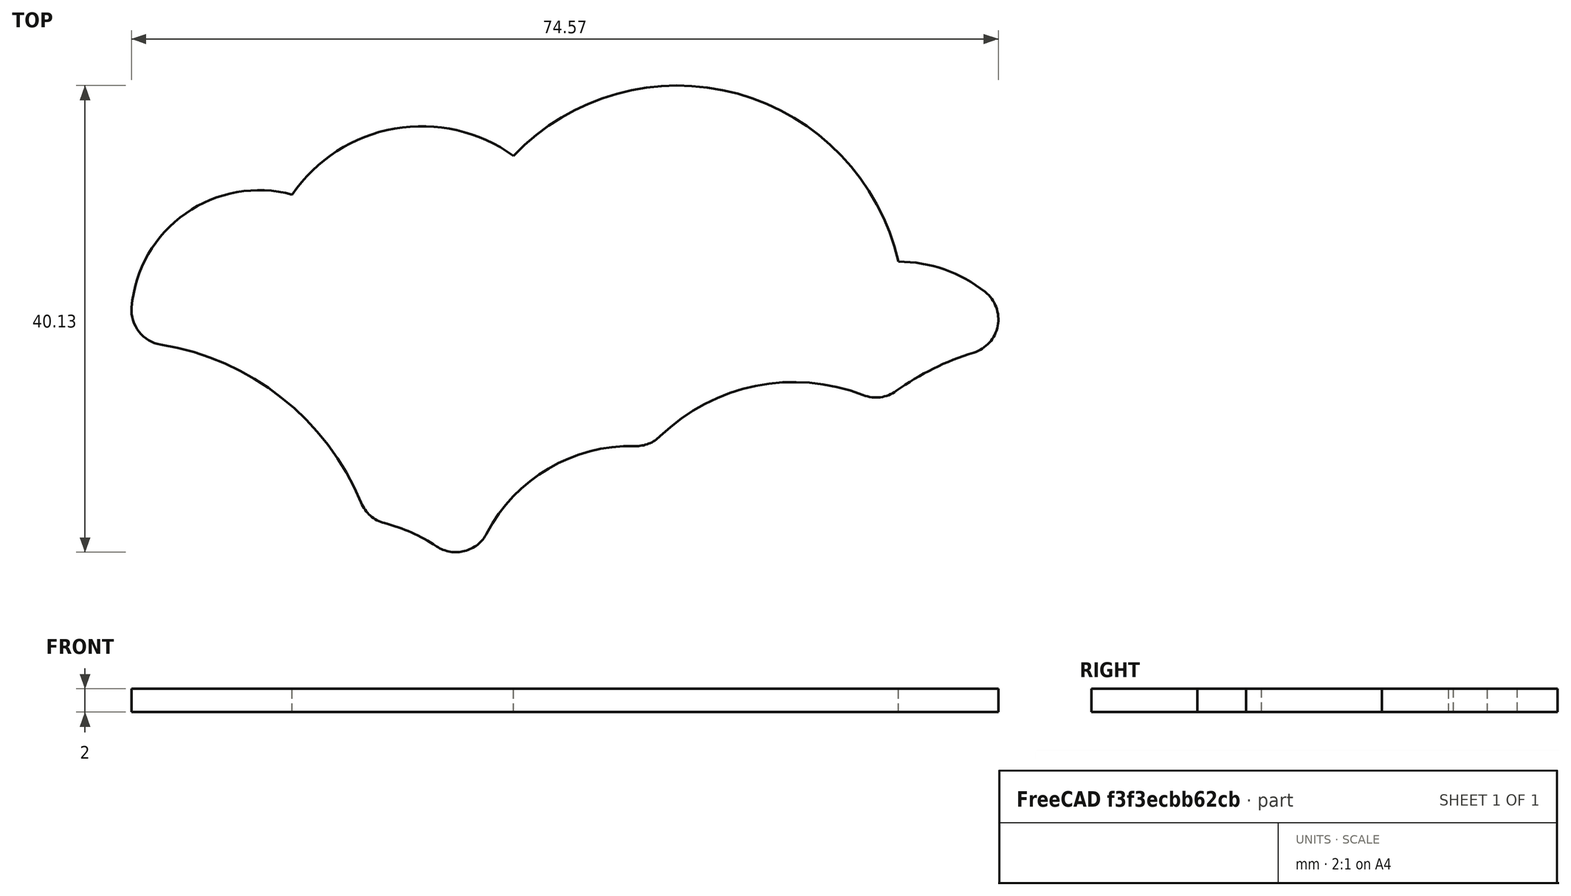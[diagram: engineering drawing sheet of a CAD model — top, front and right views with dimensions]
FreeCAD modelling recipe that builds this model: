
FCSTD DOCUMENT  (FreeCAD 0.16R6712 (Git))
Label: steam_badge2
License: All rights reserved
LicenseURL: http://en.wikipedia.org/wiki/All_rights_reserved
objects: Sketcher::SketchObject×1, Part::Feature×1, PartDesign::Pad×1
note: 4 computed .brp shape members not serialized (recipe doc carries the construction recipe); baked Part::Feature solids carry a one-line shape summary decoded from their .brp

FEATURE [Sketcher::SketchObject] Sketch
  sketch-geometry (15):
    g0: ArcOfCircle CenterX=-28 CenterY=3.5 CenterZ=0 NormalX=0 NormalY=0 NormalZ=1 Radius=11 StartAngle=1.30799 EndAngle=3.05653
    g1: ArcOfCircle CenterX=-14 CenterY=6.5 CenterZ=0 NormalX=0 NormalY=0 NormalZ=1 Radius=13.5 StartAngle=0.946866 EndAngle=2.54163
    g2: ArcOfCircle CenterX=8 CenterY=4 CenterZ=0 NormalX=0 NormalY=0 NormalZ=1 Radius=19.5 StartAngle=0.225496 EndAngle=2.38
    g3: ArcOfCircle CenterX=27 CenterY=-3.64 CenterZ=0 NormalX=0 NormalY=0 NormalZ=1 Radius=12 StartAngle=0.898843 EndAngle=1.57027
    g4: ArcOfCircle CenterX=-40 CenterY=-21 CenterZ=0 NormalX=0 NormalY=0 NormalZ=1 Radius=22.5 StartAngle=0.393398 EndAngle=1.41213
    g5: ArcOfCircle CenterX=-21 CenterY=-28.64 CenterZ=0 NormalX=0 NormalY=0 NormalZ=1 Radius=15 StartAngle=0.986285 EndAngle=1.31513
    g6: ArcOfCircle CenterX=4 CenterY=-21.5 CenterZ=0 NormalX=0 NormalY=0 NormalZ=1 Radius=14 StartAngle=1.54604 EndAngle=2.66017
    g7: ArcOfCircle CenterX=18 CenterY=-18.5 CenterZ=0 NormalX=0 NormalY=0 NormalZ=1 Radius=16.5 StartAngle=1.19974 EndAngle=2.34113
    g8: ArcOfCircle CenterX=40 CenterY=-21 CenterZ=0 NormalX=0 NormalY=0 NormalZ=1 Radius=22.5 StartAngle=1.86512 EndAngle=2.19624
    g9: ArcOfCircle CenterX=-35.9711 CenterY=4.17971 CenterZ=0 NormalX=0 NormalY=0 NormalZ=1 Radius=3 StartAngle=3.05653 EndAngle=4.55373
    g10: ArcOfCircle CenterX=-11.0677 CenterY=-13.6283 CenterZ=0 NormalX=0 NormalY=0 NormalZ=1 Radius=3 StartAngle=4.12788 EndAngle=5.80176
    g11: ArcOfCircle CenterX=32.6026 CenterY=3.40346 CenterZ=0 NormalX=0 NormalY=0 NormalZ=1 Radius=3 StartAngle=5.00671 EndAngle=7.18203
    g12: ArcOfCircle CenterX=-16.4479 CenterY=-11.2251 CenterZ=0 NormalX=0 NormalY=0 NormalZ=1 Radius=3 StartAngle=3.53499 EndAngle=4.45672
    g13: ArcOfCircle CenterX=4.42076 CenterY=-4.50521 CenterZ=0 NormalX=0 NormalY=0 NormalZ=1 Radius=3 StartAngle=4.68764 EndAngle=5.48272
    g14: ArcOfCircle CenterX=25.0708 CenterY=-0.327107 CenterZ=0 NormalX=0 NormalY=0 NormalZ=1 Radius=3 StartAngle=4.34133 EndAngle=5.33784
  constraints (60):
    c: Radius(g0) = 11
    c: Radius(g1) = 13.5
    c: Radius(g2) = 19.5
    c: Radius(g3) = 12
    c: Coincident(g0,g1)
    c: Coincident(g1,g2)
    c: Coincident(g2,g3)
    c: Radius(g4) = 22.5
    c: Radius(g5) = 15
    c: Radius(g6) = 14
    c: Radius(g7) = 16.5
    c: Radius(g8) = 22.5
    c: DistanceY(g-1,g0) = 3.5
    c: DistanceY(g-1,g1) = 6.5
    c: DistanceY(g-1,g2) = 4
    c: DistanceY(g8,g-1) = 21
    c: DistanceY(g7,g-1) = 18.5
    c: DistanceY(g6,g-1) = 21.5
    c: DistanceY(g4,g-1) = 21
    c: DistanceX(g-1,g2) = 8
    c: DistanceX(g-1,g3) = 27
    c: DistanceX(g-1,g8) = 40
    c: DistanceX(g-1,g7) = 18
    c: DistanceX(g-1,g6) = 4
    c: DistanceX(g5) = -21
    c: DistanceX(g4,g-1) = 40
    c: DistanceX(g0,g-1) = 28
    c: DistanceX(g1,g-1) = 14
    c: DistanceY(g3,g-1) = 3.64
    c: DistanceY(g5,g-1) = 28.64
    c: Radius(g9) = 3
    c: Tangent(g9,g4)
    c: Tangent(g9,g0)
    c: Coincident(g4,g9)
    c: Coincident(g0,g9)
    c: Radius(g10) = 3
    c: Tangent(g10,g6)
    c: Tangent(g10,g5)
    c: Coincident(g6,g10)
    c: Coincident(g5,g10)
    c: Radius(g11) = 3
    c: Tangent(g11,g3)
    c: Tangent(g11,g8)
    c: Coincident(g8,g11)
    c: Coincident(g3,g11)
    c: Radius(g12) = 3
    c: Tangent(g12,g5)
    c: Tangent(g12,g4)
    c: Coincident(g5,g12)
    c: Coincident(g4,g12)
    c: Radius(g13) = 3
    c: Tangent(g13,g7)
    c: Tangent(g13,g6)
    c: Coincident(g7,g13)
    c: Coincident(g6,g13)
    c: Radius(g14) = 3
    c: Tangent(g14,g8)
    c: Tangent(g14,g7)
    c: Coincident(g7,g14)
    c: Coincident(g8,g14)
FEATURE [Part::Feature] Sketch001
  shape: bbox 76.89 x 42.25 x 2e-07 mm, 0 faces, 0 solids (baked)
FEATURE [PartDesign::Pad] Pad
  Length = 2
  Length2 = 100
  Sketch = -> Sketch
  Type = 0
